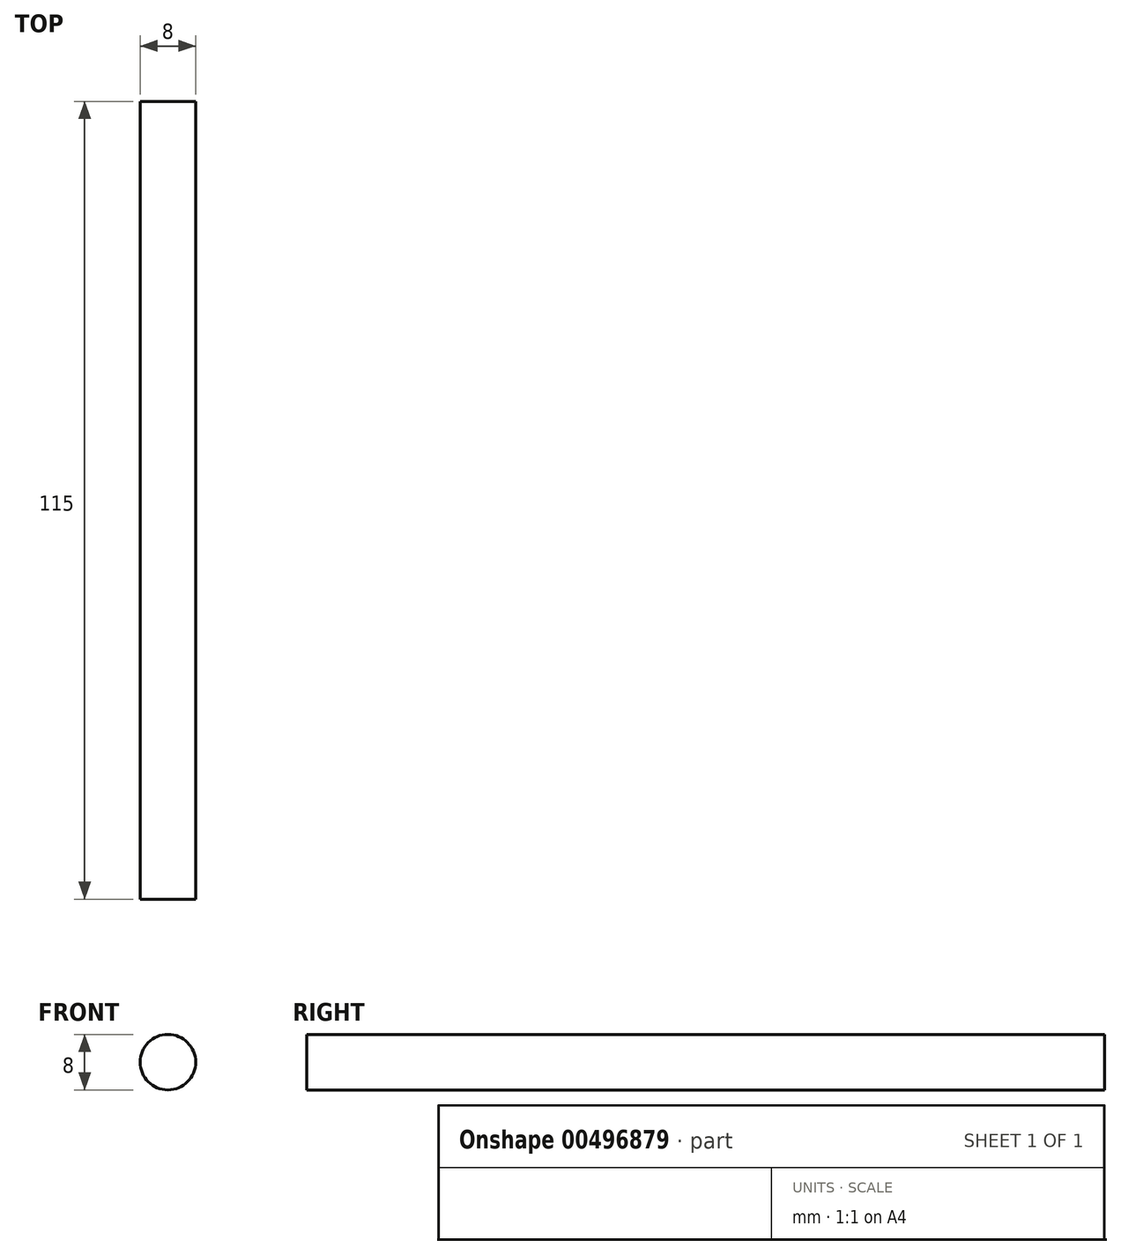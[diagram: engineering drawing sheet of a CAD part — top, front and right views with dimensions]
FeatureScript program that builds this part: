
annotation { "Feature Type Name" : "Feature", "Feature Type Description" : "" }
export const myFeature = defineFeature(function(context is Context, id is Id, definition is map)
    precondition{}
    {
        {
            var Q0;
            Q0=qCreatedBy(makeId("Front.planeOp"),FACE);
            var sketch = newSketch(context, id + "F0", { "sketchPlane" : qUnion([Q0])});
            skCircle(sketch, "E0", {"center": v(0, 0) * mm, "radius": 4 * mm});
            skSolve(sketch);
        }
        {
            var Q0;
            Q0 = qSketchRegion(id + "F0", true);
            extrude(context, id + "F1", {"entities" : qUnion([Q0]), "depth" : 115 * mm});
        }
    });
